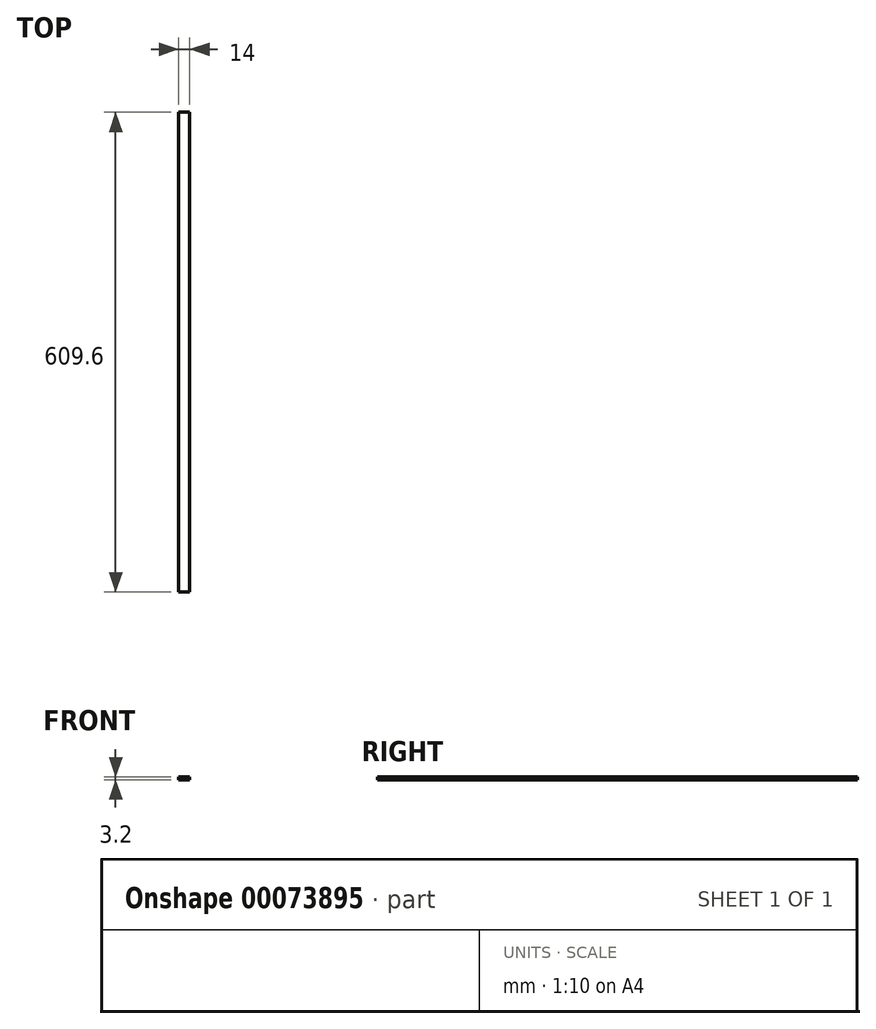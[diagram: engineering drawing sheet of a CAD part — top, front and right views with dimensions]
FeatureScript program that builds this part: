
annotation { "Feature Type Name" : "Feature", "Feature Type Description" : "" }
export const myFeature = defineFeature(function(context is Context, id is Id, definition is map)
    precondition{}
    {
        {
            var Q0;
            Q0=qCreatedBy(makeId("Top.planeOp"),FACE);
            var sketch = newSketch(context, id + "F0", { "sketchPlane" : qUnion([Q0])});
            skLineSegment(sketch, "E0.bottom", {"start": v(-14, 304.8) * mm, "end": v(0, 304.8) * mm});
            skLineSegment(sketch, "E0.top", {"start": v(-14, -304.8) * mm, "end": v(0, -304.8) * mm});
            skLineSegment(sketch, "E0.left", {"start": v(-14, 304.8) * mm, "end": v(-14, -304.8) * mm});
            skLineSegment(sketch, "E0.right", {"start": v(0, 304.8) * mm, "end": v(0, -304.8) * mm});
            skSolve(sketch);
        }
        {
            var Q0;
            Q0=makeQuery(id+"F0.imprint","IMPRINT",FACE,{"disambiguationData":[TD([[makeQuery(id+"F0.imprint","IMPRINT",EDGE,{"derivedFrom":sQuery(id+"F0.wireOp",EDGE,"E0.bottom")}),-1.0]])]});
            extrude(context, id + "F1", {"entities" : qUnion([Q0]), "depth" : (1.6 * 2) * mm});
        }
    });
